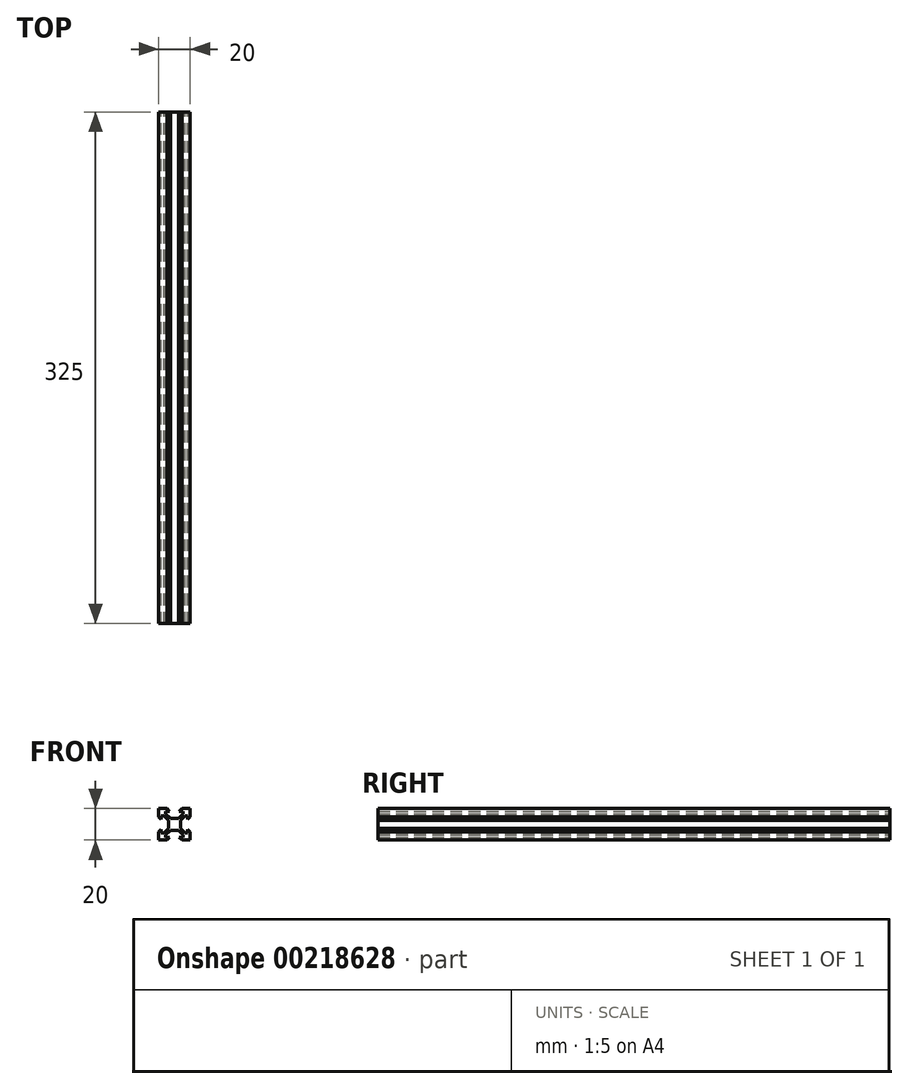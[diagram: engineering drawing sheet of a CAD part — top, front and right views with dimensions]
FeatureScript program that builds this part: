
annotation { "Feature Type Name" : "Feature", "Feature Type Description" : "" }
export const myFeature = defineFeature(function(context is Context, id is Id, definition is map)
    precondition{}
    {
        {
            var Q0;
            Q0=qCreatedBy(makeId("Front.planeOp"),FACE);
            var sketch = newSketch(context, id + "F0", { "sketchPlane" : qUnion([Q0])});
            skLineSegment(sketch, "E0", {"start": v(-10, 10) * mm, "end": v(-4.78, 10) * mm});
            skLineSegment(sketch, "E1", {"start": v(-4.78, 10) * mm, "end": v(-3.1, 8.33) * mm});
            skLineSegment(sketch, "E2", {"start": v(-3.1, 8.32) * mm, "end": v(-5.5, 8.32) * mm});
            skLineSegment(sketch, "E3", {"start": v(-5.5, 8.32) * mm, "end": v(-5.5, 6.68) * mm});
            skLineSegment(sketch, "E4", {"start": v(-5.5, 6.68) * mm, "end": v(-2.57, 3.75) * mm});
            skLineSegment(sketch, "E5", {"start": v(-2.57, 3.75) * mm, "end": v(0, 3.75) * mm});
            skLineSegment(sketch, "E6", {"start": v(0, 0) * mm, "end": v(0, -2.66) * mm, "construction": true});
            skLineSegment(sketch, "E7", {"start": v(0, 0) * mm, "end": v(-3.75, 0) * mm, "construction": true});
            skLineSegment(sketch, "E8", {"start": v(-10, 10) * mm, "end": v(-10, 4.77) * mm});
            skLineSegment(sketch, "E9", {"start": v(-10, 4.78) * mm, "end": v(-8.33, 3.1) * mm});
            skLineSegment(sketch, "E10", {"start": v(-8.32, 3.1) * mm, "end": v(-8.32, 5.5) * mm});
            skLineSegment(sketch, "E11", {"start": v(-8.33, 5.5) * mm, "end": v(-6.68, 5.5) * mm});
            skLineSegment(sketch, "E12", {"start": v(-6.68, 5.5) * mm, "end": v(-3.75, 2.57) * mm});
            skLineSegment(sketch, "E13", {"start": v(-3.75, 2.57) * mm, "end": v(-3.75, 0) * mm});
            skCircle(sketch, "E14", {"center": v(0, 0) * mm, "radius": 2.1 * mm, "construction": true});
            skLineSegment(sketch, "E15.1.0", {"start": v(-5.5, -6.68) * mm, "end": v(-2.57, -3.75) * mm});
            skLineSegment(sketch, "E15.1.1", {"start": v(-5.5, -8.33) * mm, "end": v(-5.5, -6.68) * mm});
            skLineSegment(sketch, "E15.1.2", {"start": v(-3.1, -8.32) * mm, "end": v(-5.5, -8.32) * mm});
            skLineSegment(sketch, "E15.1.3", {"start": v(-4.78, -10) * mm, "end": v(-3.1, -8.33) * mm});
            skLineSegment(sketch, "E15.1.4", {"start": v(-10, -10) * mm, "end": v(-4.77, -10) * mm});
            skLineSegment(sketch, "E15.1.5", {"start": v(-8.32, -5.5) * mm, "end": v(-6.68, -5.5) * mm});
            skLineSegment(sketch, "E15.1.6", {"start": v(-8.32, -3.1) * mm, "end": v(-8.32, -5.5) * mm});
            skLineSegment(sketch, "E15.1.7", {"start": v(-10, -4.77) * mm, "end": v(-8.33, -3.1) * mm});
            skLineSegment(sketch, "E15.1.8", {"start": v(-10, -10) * mm, "end": v(-10, -4.77) * mm});
            skLineSegment(sketch, "E15.1.9", {"start": v(-2.57, -3.75) * mm, "end": v(0, -3.75) * mm});
            skLineSegment(sketch, "E15.1.10", {"start": v(-6.68, -5.5) * mm, "end": v(-3.75, -2.57) * mm});
            skLineSegment(sketch, "E15.1.11", {"start": v(-3.75, -2.57) * mm, "end": v(-3.75, 0) * mm});
            skLineSegment(sketch, "E15.2.0", {"start": v(6.68, -5.5) * mm, "end": v(3.75, -2.57) * mm});
            skLineSegment(sketch, "E15.2.1", {"start": v(8.33, -5.5) * mm, "end": v(6.68, -5.5) * mm});
            skLineSegment(sketch, "E15.2.2", {"start": v(8.32, -3.1) * mm, "end": v(8.32, -5.5) * mm});
            skLineSegment(sketch, "E15.2.3", {"start": v(10, -4.78) * mm, "end": v(8.33, -3.1) * mm});
            skLineSegment(sketch, "E15.2.4", {"start": v(10, -10) * mm, "end": v(10, -4.78) * mm});
            skLineSegment(sketch, "E15.2.5", {"start": v(5.5, -8.32) * mm, "end": v(5.5, -6.68) * mm});
            skLineSegment(sketch, "E15.2.6", {"start": v(3.1, -8.32) * mm, "end": v(5.5, -8.32) * mm});
            skLineSegment(sketch, "E15.2.7", {"start": v(4.77, -10) * mm, "end": v(3.1, -8.33) * mm});
            skLineSegment(sketch, "E15.2.8", {"start": v(10, -10) * mm, "end": v(4.77, -10) * mm});
            skLineSegment(sketch, "E15.2.9", {"start": v(3.75, -2.57) * mm, "end": v(3.75, 0) * mm});
            skLineSegment(sketch, "E15.2.10", {"start": v(5.5, -6.68) * mm, "end": v(2.57, -3.75) * mm});
            skLineSegment(sketch, "E15.2.11", {"start": v(2.57, -3.75) * mm, "end": v(0, -3.75) * mm});
            skLineSegment(sketch, "E15.3.0", {"start": v(5.5, 6.68) * mm, "end": v(2.57, 3.75) * mm});
            skLineSegment(sketch, "E15.3.1", {"start": v(5.5, 8.33) * mm, "end": v(5.5, 6.68) * mm});
            skLineSegment(sketch, "E15.3.2", {"start": v(3.1, 8.32) * mm, "end": v(5.5, 8.32) * mm});
            skLineSegment(sketch, "E15.3.3", {"start": v(4.78, 10) * mm, "end": v(3.1, 8.33) * mm});
            skLineSegment(sketch, "E15.3.4", {"start": v(10, 10) * mm, "end": v(4.78, 10) * mm});
            skLineSegment(sketch, "E15.3.5", {"start": v(8.32, 5.5) * mm, "end": v(6.68, 5.5) * mm});
            skLineSegment(sketch, "E15.3.6", {"start": v(8.32, 3.1) * mm, "end": v(8.32, 5.5) * mm});
            skLineSegment(sketch, "E15.3.7", {"start": v(10, 4.77) * mm, "end": v(8.33, 3.1) * mm});
            skLineSegment(sketch, "E15.3.8", {"start": v(10, 10) * mm, "end": v(10, 4.77) * mm});
            skLineSegment(sketch, "E15.3.9", {"start": v(2.57, 3.75) * mm, "end": v(0, 3.75) * mm});
            skLineSegment(sketch, "E15.3.10", {"start": v(6.68, 5.5) * mm, "end": v(3.75, 2.57) * mm});
            skLineSegment(sketch, "E15.3.11", {"start": v(3.75, 2.57) * mm, "end": v(3.75, 0) * mm});
            skSolve(sketch);
        }
        {
            var Q0;
            Q0=qSketchRegion(id+"F0",true);
            extrude(context, id + "F1", {"entities" : qUnion([Q0]), "depth" : 325 * mm, "symmetric" : true});
        }
    });
